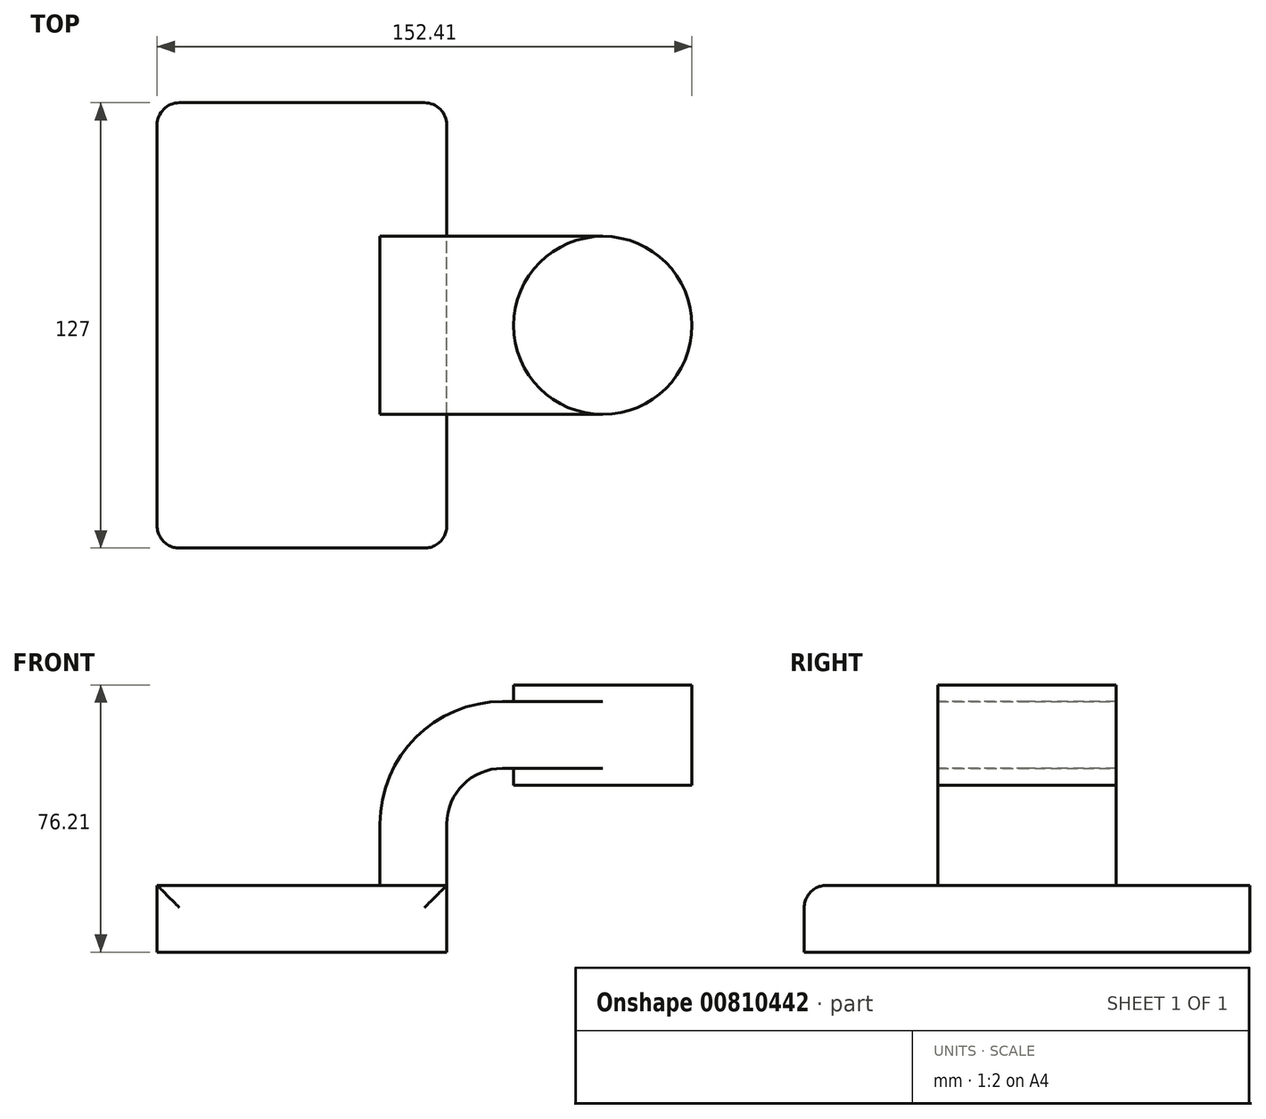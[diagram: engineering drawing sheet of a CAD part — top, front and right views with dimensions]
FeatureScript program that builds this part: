
annotation { "Feature Type Name" : "Feature", "Feature Type Description" : "" }
export const myFeature = defineFeature(function(context is Context, id is Id, definition is map)
    precondition{}
    {
        {
            var Q0;
            Q0=qCreatedBy(makeId("Front.planeOp"),FACE);
            var sketch = newSketch(context, id + "F0", { "sketchPlane" : qUnion([Q0])});
            skLineSegment(sketch, "E0.bottom", {"start": v(-41.28, 9.52) * mm, "end": v(41.28, 9.53) * mm});
            skLineSegment(sketch, "E0.top", {"start": v(-41.28, -9.53) * mm, "end": v(41.28, -9.53) * mm});
            skLineSegment(sketch, "E0.left", {"start": v(-41.28, 9.52) * mm, "end": v(-41.28, -9.53) * mm});
            skLineSegment(sketch, "E0.right", {"start": v(41.27, 9.53) * mm, "end": v(41.28, -9.52) * mm});
            skPoint(sketch, "E0.middle", {"position": v(0, 0) * mm});
            skLineSegment(sketch, "E1.bottom", {"start": v(111.12, 38.1) * mm, "end": v(60.32, 38.1) * mm});
            skLineSegment(sketch, "E1.top", {"start": v(111.12, 66.67) * mm, "end": v(60.32, 66.67) * mm});
            skLineSegment(sketch, "E1.left", {"start": v(111.12, 38.1) * mm, "end": v(111.12, 66.68) * mm});
            skLineSegment(sketch, "E1.right", {"start": v(60.32, 38.1) * mm, "end": v(60.32, 66.68) * mm});
            skPoint(sketch, "E1.middle", {"position": v(85.72, 52.39) * mm});
            skLineSegment(sketch, "E2", {"start": v(41.27, 9.53) * mm, "end": v(41.27, 27) * mm});
            skArc(sketch, "E3", {"start": v(41.27, 27) * mm, "mid": v(45.92, 38.23) * mm, "end": v(57.15, 42.88) * mm});
            skLineSegment(sketch, "E4", {"start": v(57.15, 42.88) * mm, "end": v(85.72, 42.88) * mm});
            skLineSegment(sketch, "E5.0", {"start": v(57.15, 61.93) * mm, "end": v(85.72, 61.93) * mm});
            skArc(sketch, "E5.1", {"start": v(22.23, 27) * mm, "mid": v(32.45, 51.7) * mm, "end": v(57.15, 61.93) * mm});
            skLineSegment(sketch, "E5.2", {"start": v(22.22, 9.53) * mm, "end": v(22.22, 27) * mm});
            skLineSegment(sketch, "E6", {"start": v(85.72, 38.1) * mm, "end": v(85.72, 66.67) * mm});
            skFitSpline(sketch, "E7", {"points": [v(-41.28, 9.52) * mm, v(57.15, 61.93) * mm], "startDerivative": vector(12.31, 100.47) * mm, "endDerivative": vector(107.07, -7.02) * mm});
            skSolve(sketch);
        }
        {
            var Q0;
            Q0=makeQuery(id+"F0.imprint","IMPRINT",FACE,{"disambiguationData":[TD([[makeQuery(id+"F0.imprint","IMPRINT",EDGE,{"derivedFrom":sQuery(id+"F0.wireOp",EDGE,"E0.top")}),1.0]])]});
            extrude(context, id + "F1", {"entities" : qUnion([Q0]), "endBound" : BoundingType.SYMMETRIC, "depth" : 127 * mm, "offsetDistance" : 25.4 * mm});
        }
        {
            var Q0;
            {var subQ1=sQuery(id+"F0.wireOp",EDGE,"E2");Q0=makeQuery(id+"F0.imprint","IMPRINT",FACE,{"disambiguationData":[TD([[makeQuery(id+"F0.imprint","IMPRINT",EDGE,{"derivedFrom":subQ1}),1.0]])]});}
            var Q1;
            {var subQ0=sQuery(id+"F0.wireOp",EDGE,"E4");var subQ1=sQuery(id+"F0.wireOp",EDGE,"E1.right");var subQ2=makeQuery(id+"F0.imprint","INTERSECT",VERTEX,{"derivedFrom":[subQ1,subQ0]});Q1=makeQuery(id+"F0.imprint","IMPRINT",FACE,{"disambiguationData":[TD([[makeQuery(id+"F0.imprint","IMPRINT",EDGE,{"disambiguationData":[TD([[subQ2,-1.0]])],"derivedFrom":subQ1}),-1.0]])]});}
            extrude(context, id + "F2", {"entities" : qUnion([Q0, Q1]), "endBound" : BoundingType.SYMMETRIC, "depth" : 50.8 * mm, "offsetDistance" : 25.4 * mm});
        }
        {
            var Q0;
            Q0=makeQuery(id+"F0.imprint","IMPRINT",FACE,{"disambiguationData":[TD([[makeQuery(id+"F0.imprint","IMPRINT",EDGE,{"derivedFrom":sQuery(id+"F0.wireOp",EDGE,"E5.1")}),1.0]])]});
            extrude(context, id + "F3", {"entities" : qUnion([Q0]), "endBound" : BoundingType.SYMMETRIC, "depth" : 15.88 * mm, "offsetDistance" : 25.4 * mm});
        }
        {
            var Q0;
            {var subQ4=sQuery(id+"F0.wireOp",EDGE,"E1.left");Q0=makeQuery(id+"F0.imprint","IMPRINT",FACE,{"disambiguationData":[TD([[makeQuery(id+"F0.imprint","IMPRINT",EDGE,{"derivedFrom":subQ4}),1.0]])]});}
            var Q1;
            Q1=sQuery(id+"F0.wireOp",EDGE,"E6");
            revolve(context, id + "F4", {"operationType" : NewBodyOperationType.ADD, "surfaceOperationType" : NewSurfaceOperationType.NEW, "entities" : qUnion([Q0]), "axis" : qUnion([Q1]), "revolveType" : RevolveType.FULL});
        }
        {
            var Q0;
            Q0=makeQuery(id+"F1.opExtrude","CAP_EDGE",EDGE,{"disambiguationData":[OSD([sQuery(id+"F0.wireOp",EDGE,"E0.left")])],"isStart":false});
            var Q1;
            Q1=makeQuery(id+"F1.opExtrude","CAP_EDGE",EDGE,{"disambiguationData":[OSD([sQuery(id+"F0.wireOp",EDGE,"E0.right")])],"isStart":false});
            var Q2;
            Q2=makeQuery(id+"F1.opExtrude","CAP_EDGE",EDGE,{"disambiguationData":[OSD([sQuery(id+"F0.wireOp",EDGE,"E0.right")])],"isStart":true});
            var Q3;
            Q3=makeQuery(id+"F1.opExtrude","CAP_EDGE",EDGE,{"disambiguationData":[OSD([sQuery(id+"F0.wireOp",EDGE,"E0.left")])],"isStart":true});
            var Q4;
            Q4=makeQuery(id+"F1.opExtrude","CAP_EDGE",EDGE,{"disambiguationData":[OSD([sQuery(id+"F0.wireOp",EDGE,"E0.bottom")])],"isStart":false});
            fillet(context, id + "F5", {"entities" : qUnion([Q0, Q1, Q2, Q3, Q4]), "radius" : 6.35 * mm, "tangentPropagation" : true, "allowEdgeOverflow" : false});
        }
    });
